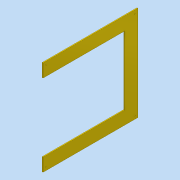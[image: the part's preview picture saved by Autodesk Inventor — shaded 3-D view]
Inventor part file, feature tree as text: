
AUTODESK INVENTOR PART (.ipt)
format: ipt  version: 2016 (Build 200138000, 138)  size: 101,888 bytes
history: native  units: mm
features: hole x4, extrude x1, sketch x1
ambient origin geometry x8: Origin, YZ Plane, XZ Plane, XY Plane, X Axis, Y Axis, Z Axis, Center Point
bodies: Solid1 (feature_tree)
feature tree (6):
  extrude  "Extrusion1"  Depth=360.0mm
  hole  "Hole1"  [1 undecoded]
  hole  "Hole2"  [1 undecoded]
  hole  "Hole3"  [1 undecoded]
  hole  "Hole4"  [1 undecoded]
  sketch  "Sketch1"  dims[d4=360.0mm d5=360.0mm d6=310.0mm d7=260.0mm d8=3.0mm d9=0.0mm d10=12.0mm d11=12.0mm d12=4.0mm d13=6.0mm d14=4.0mm d15=2.0mm d16=90.0deg d17=8.0mm d18=20.594885mm d19=12.0mm d20=12.0mm d21=4.0mm d22=6.0mm d23=4.0mm d24=2.0mm d25=90.0deg d26=8.0mm d27=20.594885mm d28=12.0mm d29=12.0mm d30=4.0mm d31=6.0mm d32=4.0mm d33=2.0mm d34=90.0deg d35=8.0mm d36=20.594885mm d37=12.0mm d38=12.0mm d39=4.0mm d40=6.0mm d41=4.0mm d42=2.0mm d43=90.0deg d44=8.0mm d45=20.594885mm]
note: 4 required parameter values undecoded (feature->parameter linkage not recoverable at this tier; creation-order binding heuristic only, values carry confidence <= 0.55)
